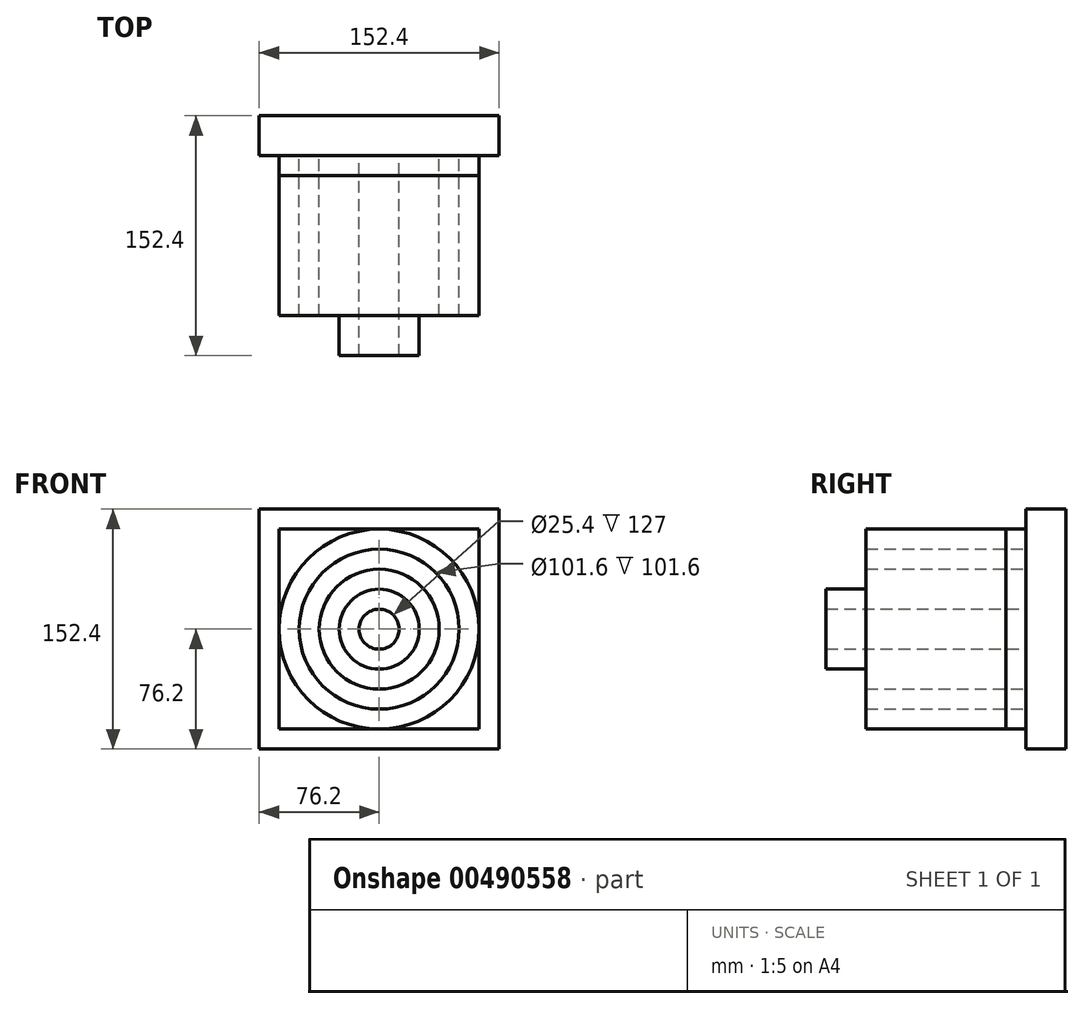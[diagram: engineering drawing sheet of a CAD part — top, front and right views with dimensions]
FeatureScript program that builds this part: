
annotation { "Feature Type Name" : "Feature", "Feature Type Description" : "" }
export const myFeature = defineFeature(function(context is Context, id is Id, definition is map)
    precondition{}
    {
        {
            var Q0;
            Q0=qCreatedBy(makeId("Front.planeOp"),FACE);
            var sketch = newSketch(context, id + "F0", { "sketchPlane" : qUnion([Q0])});
            skCircle(sketch, "E0", {"center": v(0, 0) * mm, "radius": 63.5 * mm});
            skCircle(sketch, "E1", {"center": v(0, 0) * mm, "radius": 38.1 * mm});
            skSolve(sketch);
        }
        {
            var Q0;
            Q0=makeQuery(id+"F0.imprint","IMPRINT",FACE,{"disambiguationData":[TD([[makeQuery(id+"F0.imprint","IMPRINT",EDGE,{"derivedFrom":sQuery(id+"F0.wireOp",EDGE,"E0")}),1.0]])]});
            extrude(context, id + "F1", {"entities" : qUnion([Q0]), "depth" : 12.7 * mm});
        }
        {
            var Q0;
            Q0=qCreatedBy(makeId("Front.planeOp"),FACE);
            var sketch = newSketch(context, id + "F2", { "sketchPlane" : qUnion([Q0])});
            skCircle(sketch, "E2", {"center": v(0, 0) * mm, "radius": 25.4 * mm});
            skCircle(sketch, "E3", {"center": v(0, 0) * mm, "radius": 38.1 * mm});
            skSolve(sketch);
        }
        {
            var Q0;
            Q0=makeQuery(id+"F2.imprint","IMPRINT",FACE,{"disambiguationData":[TD([[makeQuery(id+"F2.imprint","IMPRINT",EDGE,{"derivedFrom":sQuery(id+"F2.wireOp",EDGE,"E2")}),-1.0]])]});
            extrude(context, id + "F3", {"entities" : qUnion([Q0]), "operationType" : NewBodyOperationType.ADD, "depth" : 127 * mm});
        }
        {
            var Q0;
            Q0=qCreatedBy(makeId("Front.planeOp"),FACE);
            var sketch = newSketch(context, id + "F4", { "sketchPlane" : qUnion([Q0])});
            skCircle(sketch, "E4", {"center": v(0, 0) * mm, "radius": 25.4 * mm});
            skCircle(sketch, "E5", {"center": v(0, 0) * mm, "radius": 12.7 * mm});
            skSolve(sketch);
        }
        {
            var Q0;
            Q0=makeQuery(id+"F4.imprint","IMPRINT",FACE,{"disambiguationData":[TD([[makeQuery(id+"F4.imprint","IMPRINT",EDGE,{"derivedFrom":sQuery(id+"F4.wireOp",EDGE,"E4")}),1.0]])]});
            extrude(context, id + "F5", {"entities" : qUnion([Q0]), "operationType" : NewBodyOperationType.ADD, "depth" : 152.4 * mm});
        }
        {
            var Q0;
            Q0=qCreatedBy(makeId("Front.planeOp"),FACE);
            var sketch = newSketch(context, id + "F6", { "sketchPlane" : qUnion([Q0])});
            skCircle(sketch, "E6", {"center": v(0, 0) * mm, "radius": 63.5 * mm});
            skCircle(sketch, "E7", {"center": v(0, 0) * mm, "radius": 50.8 * mm});
            skSolve(sketch);
        }
        {
            var Q0;
            Q0=makeQuery(id+"F6.imprint","IMPRINT",FACE,{"disambiguationData":[TD([[makeQuery(id+"F6.imprint","IMPRINT",EDGE,{"derivedFrom":sQuery(id+"F6.wireOp",EDGE,"E6")}),1.0]])]});
            extrude(context, id + "F7", {"entities" : qUnion([Q0]), "operationType" : NewBodyOperationType.ADD, "depth" : 127 * mm});
        }
        {
            var Q0;
            Q0=qCreatedBy(makeId("Front.planeOp"),FACE);
            var sketch = newSketch(context, id + "F8", { "sketchPlane" : qUnion([Q0])});
            skLineSegment(sketch, "E8.bottom", {"start": v(76.2, 76.2) * mm, "end": v(-76.2, 76.2) * mm});
            skLineSegment(sketch, "E8.top", {"start": v(76.2, -76.2) * mm, "end": v(-76.2, -76.2) * mm});
            skLineSegment(sketch, "E8.left", {"start": v(76.2, 76.2) * mm, "end": v(76.2, -76.2) * mm});
            skLineSegment(sketch, "E8.right", {"start": v(-76.2, 76.2) * mm, "end": v(-76.2, -76.2) * mm});
            skSolve(sketch);
        }
        {
            var Q0;
            Q0=makeQuery(id+"F8.imprint","IMPRINT",FACE,{"disambiguationData":[TD([[makeQuery(id+"F8.imprint","IMPRINT",EDGE,{"derivedFrom":sQuery(id+"F8.wireOp",EDGE,"E8.bottom")}),1.0]])]});
            extrude(context, id + "F9", {"entities" : qUnion([Q0]), "operationType" : NewBodyOperationType.ADD, "depth" : 25.4 * mm});
        }
        {
            var Q0;
            {var subQ0=sQuery(id+"F8.wireOp",EDGE,"E8.top");var subQ1=sQuery(id+"F8.wireOp",EDGE,"E8.bottom");var subQ2=sQuery(id+"F8.wireOp",EDGE,"E8.left");var subQ3=sQuery(id+"F8.wireOp",EDGE,"E8.right");Q0=makeQuery(id+"F9.boolean.opBoolean","SPLIT",FACE,{"disambiguationData":[TD([makeQuery(id+"F1.opExtrude","SWEPT_FACE",FACE,{"disambiguationData":[OSD([sQuery(id+"F0.wireOp",EDGE,"E0")])]})])],"derivedFrom":makeQuery(id+"F9.opExtrude","CAP_FACE",FACE,{"disambiguationData":[OSD([subQ1,subQ0,subQ2,subQ3])],"isStart":false})});}
            var sketch = newSketch(context, id + "F10", { "sketchPlane" : qUnion([Q0])});
            skLineSegment(sketch, "E9.bottom", {"start": v(-63.5, 63.5) * mm, "end": v(63.5, 63.5) * mm});
            skLineSegment(sketch, "E9.top", {"start": v(-63.5, -63.5) * mm, "end": v(63.5, -63.5) * mm});
            skLineSegment(sketch, "E9.left", {"start": v(-63.5, 63.5) * mm, "end": v(-63.5, -63.5) * mm});
            skLineSegment(sketch, "E9.right", {"start": v(63.5, 63.5) * mm, "end": v(63.5, -63.5) * mm});
            skSolve(sketch);
        }
        {
            var Q0;
            {var subQ0=sQuery(id+"F10.wireOp",EDGE,"E9.left");var subQ1=sQuery(id+"F10.wireOp",EDGE,"E9.bottom");var subQ2=makeQuery(id+"F10.imprint","INTERSECT",VERTEX,{"derivedFrom":[subQ1,subQ0]});Q0=makeQuery(id+"F10.imprint","IMPRINT",FACE,{"disambiguationData":[TD([[makeQuery(id+"F10.imprint","IMPRINT",EDGE,{"disambiguationData":[TD([[subQ2,-1.0]])],"derivedFrom":subQ1}),-1.0]])]});}
            var Q1;
            {var subQ0=sQuery(id+"F10.wireOp",EDGE,"E9.left");var subQ1=sQuery(id+"F10.wireOp",EDGE,"E9.top");var subQ2=makeQuery(id+"F10.imprint","INTERSECT",VERTEX,{"derivedFrom":[subQ1,subQ0]});Q1=makeQuery(id+"F10.imprint","IMPRINT",FACE,{"disambiguationData":[TD([[makeQuery(id+"F10.imprint","IMPRINT",EDGE,{"disambiguationData":[TD([[subQ2,-1.0]])],"derivedFrom":subQ1}),1.0]])]});}
            var Q2;
            {var subQ0=sQuery(id+"F10.wireOp",EDGE,"E9.right");var subQ1=sQuery(id+"F10.wireOp",EDGE,"E9.bottom");var subQ2=makeQuery(id+"F10.imprint","INTERSECT",VERTEX,{"derivedFrom":[subQ1,subQ0]});Q2=makeQuery(id+"F10.imprint","IMPRINT",FACE,{"disambiguationData":[TD([[makeQuery(id+"F10.imprint","IMPRINT",EDGE,{"disambiguationData":[TD([[subQ2,1.0]])],"derivedFrom":subQ1}),-1.0]])]});}
            var Q3;
            {var subQ0=sQuery(id+"F10.wireOp",EDGE,"E9.right");var subQ1=sQuery(id+"F10.wireOp",EDGE,"E9.top");var subQ2=makeQuery(id+"F10.imprint","INTERSECT",VERTEX,{"derivedFrom":[subQ1,subQ0]});Q3=makeQuery(id+"F10.imprint","IMPRINT",FACE,{"disambiguationData":[TD([[makeQuery(id+"F10.imprint","IMPRINT",EDGE,{"disambiguationData":[TD([[subQ2,1.0]])],"derivedFrom":subQ1}),1.0]])]});}
            extrude(context, id + "F11", {"entities" : qUnion([Q0, Q1, Q2, Q3]), "operationType" : NewBodyOperationType.ADD, "depth" : 12.7 * mm});
        }
    });
